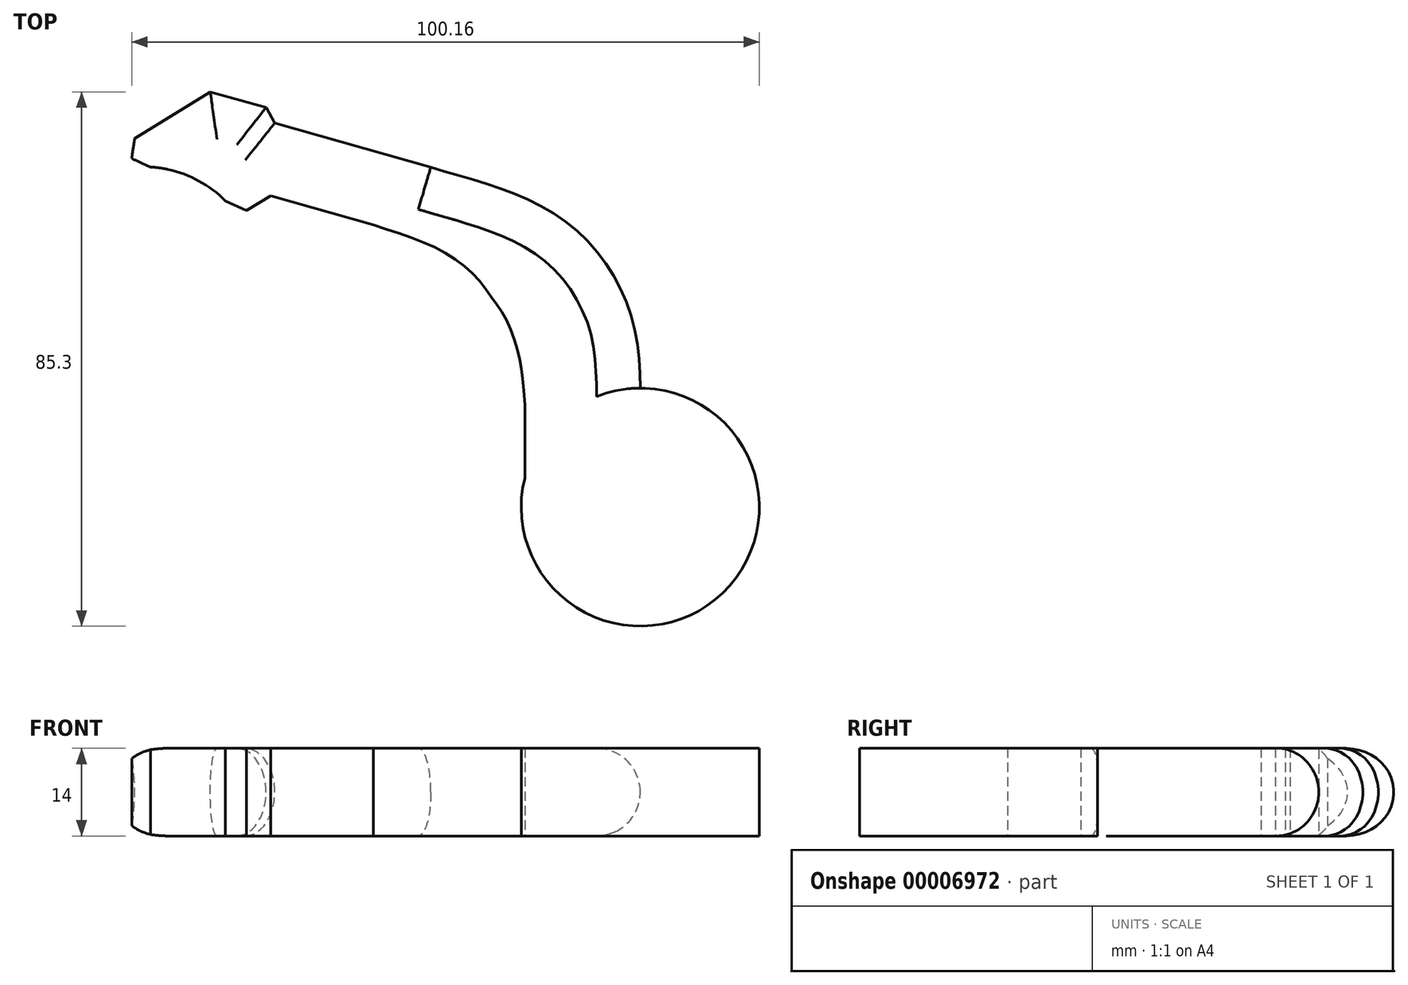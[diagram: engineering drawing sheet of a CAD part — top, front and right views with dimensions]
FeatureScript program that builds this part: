
annotation { "Feature Type Name" : "Feature", "Feature Type Description" : "" }
export const myFeature = defineFeature(function(context is Context, id is Id, definition is map)
    precondition{}
    {
        {
            var Q0;
            Q0=qCreatedBy(makeId("Top.planeOp"),FACE);
            var sketch = newSketch(context, id + "F0", { "sketchPlane" : qUnion([Q0])});
            skArc(sketch, "E0", {"start": v(-18.43, 4.63) * mm, "mid": v(11.68, -14.98) * mm, "end": v(0, 19) * mm});
            skLineSegment(sketch, "E1", {"start": v(-80.7, 58.88) * mm, "end": v(-68.63, 66.3) * mm});
            skLineSegment(sketch, "E2", {"start": v(-68.63, 66.3) * mm, "end": v(-59.7, 63.82) * mm});
            skLineSegment(sketch, "E3", {"start": v(-59.7, 63.82) * mm, "end": v(-58.33, 61.35) * mm});
            skLineSegment(sketch, "E4", {"start": v(-58.33, 61.35) * mm, "end": v(-33.44, 54.27) * mm});
            skLineSegment(sketch, "E5", {"start": v(0, 19) * mm, "end": v(0, 0) * mm});
            skLineSegment(sketch, "E6", {"start": v(-80.7, 58.88) * mm, "end": v(-81.16, 55.67) * mm});
            skLineSegment(sketch, "E7", {"start": v(-81.16, 55.67) * mm, "end": v(-78.15, 54.3) * mm});
            skLineSegment(sketch, "E8", {"start": v(-62.83, 47.38) * mm, "end": v(-58.99, 49.7) * mm});
            skLineSegment(sketch, "E9", {"start": v(-58.99, 49.7) * mm, "end": v(-42.58, 45.07) * mm});
            skLineSegment(sketch, "E10", {"start": v(-18.43, 16.3) * mm, "end": v(-18.43, 4.63) * mm});
            skArc(sketch, "E11", {"start": v(-66.23, 48.91) * mm, "mid": v(-71.7, 52.7) * mm, "end": v(-78.15, 54.3) * mm});
            skFitSpline(sketch, "E12", {"points": [v(-33.44, 54.27) * mm, v(-22.87, 51.08) * mm, v(-13.66, 46.8) * mm, v(-7.33, 41.3) * mm, v(-3.54, 35.62) * mm, v(-1.16, 29.53) * mm, v(0, 19) * mm], "startDerivative": vector(52.87, -16) * mm, "endDerivative": vector(0, -65.65) * mm});
            skPoint(sketch, "E13.orphan", {"position": v(0, 44.75) * mm});
            skFitSpline(sketch, "E14", {"points": [v(-42.58, 45.07) * mm, v(-33.64, 41.87) * mm, v(-27.23, 37.76) * mm, v(-23.69, 33.48) * mm, v(-21.06, 29.29) * mm, v(-19.25, 23.53) * mm, v(-18.43, 16.3) * mm], "startDerivative": vector(46.77, -16.08) * mm, "endDerivative": vector(4.3, -61.62) * mm});
            skLineSegment(sketch, "E15.trimOffspring", {"start": v(-66.23, 48.91) * mm, "end": v(-62.83, 47.38) * mm});
            skPoint(sketch, "E16.orphan", {"position": v(-18.43, 0) * mm});
            skSolve(sketch);
        }
        {
            var Q0;
            Q0=qSketchRegion(id+"F0",true);
            extrude(context, id + "F1", {"entities" : qUnion([Q0]), "depth" : 14 * mm});
        }
        {
            var Q0;
            Q0=makeQuery(id+"F1.opExtrude","CAP_EDGE",EDGE,{"disambiguationData":[OSD([sQuery(id+"F0.wireOp",EDGE,"E12")])],"isStart":false});
            var Q1;
            Q1=makeQuery(id+"F1.opExtrude","CAP_EDGE",EDGE,{"disambiguationData":[OSD([sQuery(id+"F0.wireOp",EDGE,"E1")])],"isStart":false});
            var Q2;
            Q2=makeQuery(id+"F1.opExtrude","CAP_EDGE",EDGE,{"disambiguationData":[OSD([sQuery(id+"F0.wireOp",EDGE,"E2")])],"isStart":false});
            var Q3;
            Q3=makeQuery(id+"F1.opExtrude","CAP_EDGE",EDGE,{"disambiguationData":[OSD([sQuery(id+"F0.wireOp",EDGE,"E3")])],"isStart":false});
            var Q4;
            Q4=makeQuery(id+"F1.opExtrude","CAP_EDGE",EDGE,{"disambiguationData":[OSD([sQuery(id+"F0.wireOp",EDGE,"E4")])],"isStart":false});
            var Q5;
            Q5=makeQuery(id+"F1.opExtrude","CAP_EDGE",EDGE,{"disambiguationData":[OSD([sQuery(id+"F0.wireOp",EDGE,"E12")])],"isStart":true});
            var Q6;
            Q6=makeQuery(id+"F1.opExtrude","CAP_EDGE",EDGE,{"disambiguationData":[OSD([sQuery(id+"F0.wireOp",EDGE,"E4")])],"isStart":true});
            var Q7;
            Q7=makeQuery(id+"F1.opExtrude","CAP_EDGE",EDGE,{"disambiguationData":[OSD([sQuery(id+"F0.wireOp",EDGE,"E3")])],"isStart":true});
            var Q8;
            Q8=makeQuery(id+"F1.opExtrude","CAP_EDGE",EDGE,{"disambiguationData":[OSD([sQuery(id+"F0.wireOp",EDGE,"E2")])],"isStart":true});
            var Q9;
            Q9=makeQuery(id+"F1.opExtrude","CAP_EDGE",EDGE,{"disambiguationData":[OSD([sQuery(id+"F0.wireOp",EDGE,"E1")])],"isStart":true});
            fillet(context, id + "F2", {"entities" : qUnion([Q0, Q1, Q2, Q3, Q4, Q5, Q6, Q7, Q8, Q9]), "radius" : 7 * mm, "tangentPropagation" : true, "allowEdgeOverflow" : false});
        }
    });
